# Revit family: Backflow_Preventer-RP-Zurn_Wilkins-Model_475DA_475DAG-(4-6_Inch)
name_source: partatom
category: Pipe Accessories
units: mm (PartAtom-declared; Revit-internal decimal feet)

## family parameters
Always vertical = Yes
Cut with Voids When Loaded = No
OmniClass Number = 23.65.55.14.21
OmniClass Title = Non-Return Valves for Liquid Services
Part Type = Valve - Breaks Into
Round Connector Dimension = Use Radius
Shared = No
Work Plane-Based = No

## types (4) — shared parameters
Assembly Code = D2020300
Bend Radius = 1 1/4"
Bend Radius Outside = 2 3/8"
Default Elevation = 0"
Description = Reduced Pressure Detector Assembly
Flow Rate (GPM) = 0 GPM
Gate Valve distance = 5 11/16"
Hydrostatic Test Pressure = 350.00 psi
MR gate valve dia-1 = 3"
MR stem dia = 1 3/8"
MR test cock dia = 1 15/16"
Main Material = Paint - Zurn - Ductile Iron - Blue
Manufacturer = Zurn Water, LLC
Manufacturer Brand = Zurn Wilkins
Max Working Water Pressure = 175.00 psi
Max Working Water Temperature = 140 °F
Modified Date = 07/17/2025
Pipe Size = 1"
Product Documentation Link = https://files.zurn.com
Product Installation Sheet URL = https://files.zurn.com
Product Page URL = https://www.zurn.com
Product data URL = https://www.bimobject.com
Repair Parts URL = https://files.zurn.com
URL = https://www.zurn.com

## per-type parameters (varying)
- 4-475DA (4" 475DA Flanged): Body outer=28 13/16"; Bypass=Bypass 475DA(4-6_inch) : 4"; DA Front=3 3/4"; DA Height From center=11"; DIM A - Inlet center to outlet center=18 5/16"; DIM B - Overall height of the  valve=30"; DIM C - Valve center to gate valve stem top=22 3/4"; DIM D - Valve center to end=8"; Gate Valve=Gate Valve_475OSY 4in : 4"; Height=30"; Length=18 5/16"; MR Right End=1 1/16"; MR Yoke Radius=1 7/8"; MR body dia-1=8"; MR center to body left side-1=5 1/4"; MR center to body left side-11=3 3/8"; MR center to body right side-1=2 1/16"; MR center to body right side-2=5 3/16"; MR center to body right side-3=5 1/4"; MR center to body right side-4=4 13/16"; MR center to gate valve-1=6 3/16"; MR center to gate valve-2=7 13/16"; MR center to gate valve-3=15 9/16"; MR center to gate valve-4=17 1/8"; MR center to main body -1=5"; MR center to main body -2=5"; MR center to main body -3=2 7/8"; MR flange dia-1=9 1/8"; MR flange dia-2=14"; MR gate valve dia-2=7"; MR gate valve dia-3=9"; MR gate valve handwheel dia=10 1/4"; Main Body=Main Body 475 4&6 : 4"; Model=475DA; Nominal Diameter=4"; Nominal Radius=2"; Overall Height=30"; Overall Length=18 5/16"; Pipe Position=6 3/8"; Pipe Vertical Position=7 1/4"; Pressure Loss at Rated Flow=10.20 psi; Product Weight (lbs)=303; Rated Flow=500 GPM
- 6-475DAG (6" 475DA Grooved): Body outer=31"; Bypass=Bypass 475DA(4-6_inch) : 6"; DA Front=4 3/4"; DA Height From center=12"; DIM A - Inlet center to outlet center=18 11/16"; DIM B - Overall height of the  valve=35 1/2"; DIM C - Valve center to gate valve stem top=30 1/8"; DIM D - Valve center to end=10"; Gate Valve=Gate Valve_475OSY 4in : 6" G; Height=35 1/2"; Length=18 11/16"; MR Right End=2 3/16"; MR Yoke Radius=2 9/16"; MR body dia-1=10 7/16"; MR center to body left side-1=3 7/8"; MR center to body left side-11=2"; MR center to body right side-1=2 1/16"; MR center to body right side-2=6 3/4"; MR center to body right side-3=5 1/4"; MR center to body right side-4=5 11/16"; MR center to gate valve-1=7 3/8"; MR center to gate valve-2=9"; MR center to gate valve-3=21 5/8"; MR center to gate valve-4=23 1/8"; MR center to main body -1=5 1/2"; MR center to main body -2=6"; MR center to main body -3=2 3/16"; MR flange dia-1=10 1/2"; MR flange dia-2=14"; MR gate valve dia-2=9"; MR gate valve dia-3=11"; MR gate valve handwheel dia=12 1/2"; Main Body=Main Body 475 4&6 : 6"; Model=475DAG; Nominal Diameter=6"; Nominal Radius=3"; Overall Height=35 1/2"; Overall Length=18 11/16"; Pipe Position=8 3/4"; Pipe Vertical Position=6 1/4"; Pressure Loss at Rated Flow=10.90 psi; Product Weight (lbs)=465; Rated Flow=1000 GPM
- 6-475DA (6" 475DA Flanged): Body outer=31"; Bypass=Bypass 475DA(4-6_inch) : 6"; DA Front=4 3/4"; DA Height From center=12"; DIM A - Inlet center to outlet center=18 11/16"; DIM B - Overall height of the  valve=35 1/2"; DIM C - Valve center to gate valve stem top=30 1/8"; DIM D - Valve center to end=10"; Gate Valve=Gate Valve_475OSY 4in : 6"; Height=35 1/2"; Length=18 11/16"; MR Right End=2 3/16"; MR Yoke Radius=2 9/16"; MR body dia-1=10 7/16"; MR center to body left side-1=3 9/16"; MR center to body left side-11=2 1/8"; MR center to body right side-1=3 1/8"; MR center to body right side-2=6 13/16"; MR center to body right side-3=5 11/16"; MR center to body right side-4=5 11/16"; MR center to gate valve-1=7 3/8"; MR center to gate valve-2=9"; MR center to gate valve-3=21 5/8"; MR center to gate valve-4=23 1/8"; MR center to main body -1=5 7/8"; MR center to main body -2=6"; MR center to main body -3=3 1/4"; MR flange dia-1=11 1/8"; MR flange dia-2=14 3/16"; MR gate valve dia-2=9"; MR gate valve dia-3=11"; MR gate valve handwheel dia=12 1/2"; Main Body=Main Body 475 4&6 : 6"; Model=475DA; Nominal Diameter=6"; Nominal Radius=3"; Overall Height=35 1/2"; Overall Length=18 11/16"; Pipe Position=8 3/4"; Pipe Vertical Position=6 1/4"; Pressure Loss at Rated Flow=10.90 psi; Product Weight (lbs)=487; Rated Flow=1000 GPM
- 4-475DAG (4" 475DA Grooved): Body outer=28 13/16"; Bypass=Bypass 475DA(4-6_inch) : 4"; DA Front=3 3/4"; DA Height From center=11"; DIM A - Inlet center to outlet center=18 5/16"; DIM B - Overall height of the  valve=30"; DIM C - Valve center to gate valve stem top=22 3/4"; DIM D - Valve center to end=8"; Gate Valve=Gate Valve_475OSY 4in : 4" G; Height=30"; Length=18 5/16"; MR Right End=1 1/16"; MR Yoke Radius=1 7/8"; MR body dia-1=8"; MR center to body left side-1=5 1/4"; MR center to body left side-11=3 3/8"; MR center to body right side-1=2 1/16"; MR center to body right side-2=5 3/16"; MR center to body right side-3=5 1/4"; MR center to body right side-4=4 13/16"; MR center to gate valve-1=6 3/16"; MR center to gate valve-2=7 13/16"; MR center to gate valve-3=15 9/16"; MR center to gate valve-4=17 1/8"; MR center to main body -1=5"; MR center to main body -2=5"; MR center to main body -3=2 7/8"; MR flange dia-1=8 1/4"; MR flange dia-2=14"; MR gate valve dia-2=7"; MR gate valve dia-3=9"; MR gate valve handwheel dia=10 1/4"; Main Body=Main Body 475 4&6 : 4"; Model=475DAG; Nominal Diameter=4"; Nominal Radius=2"; Overall Height=30"; Overall Length=18 5/16"; Pipe Position=6 3/8"; Pipe Vertical Position=7 1/4"; Pressure Loss at Rated Flow=10.20 psi; Product Weight (lbs)=279; Rated Flow=500 GPM

## geometry (parser evidence)
native form markers: Sweep x12
no freeform markers — native parametric forms only
